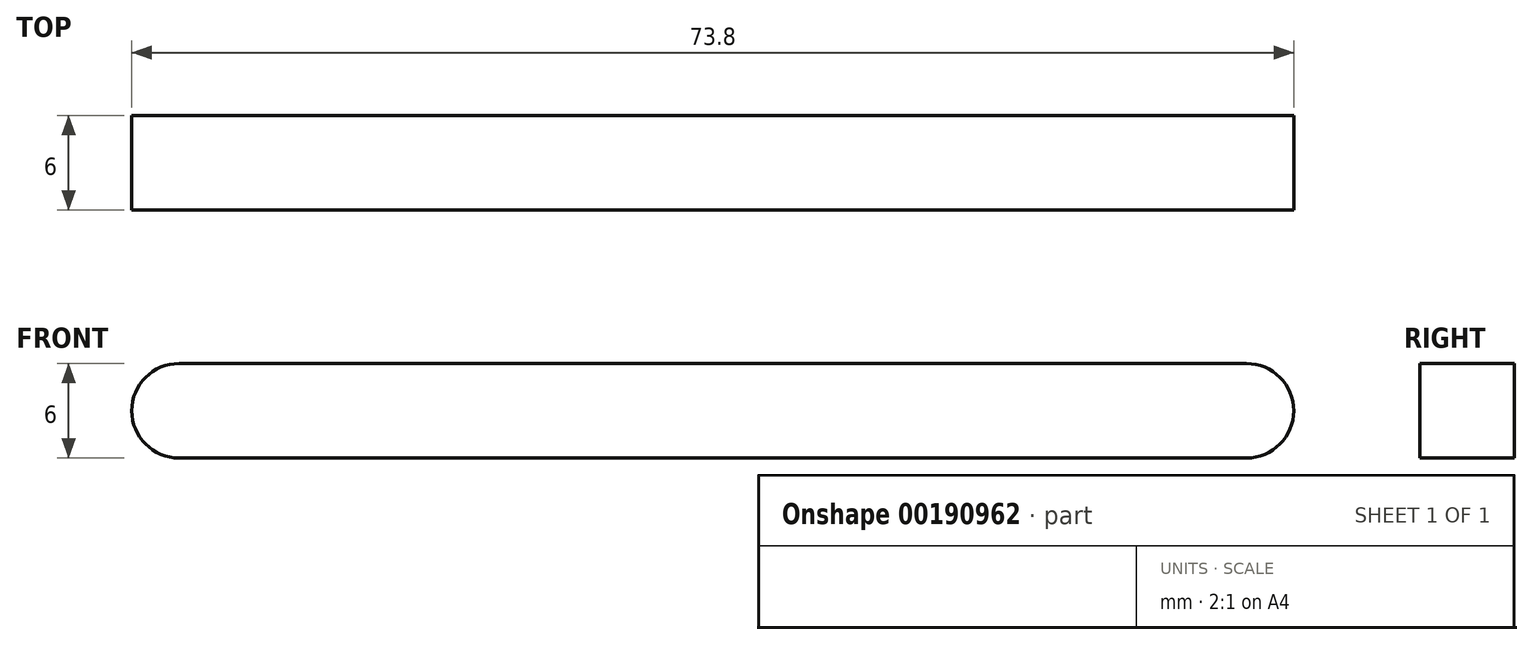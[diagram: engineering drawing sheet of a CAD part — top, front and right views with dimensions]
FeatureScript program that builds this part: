
annotation { "Feature Type Name" : "Feature", "Feature Type Description" : "" }
export const myFeature = defineFeature(function(context is Context, id is Id, definition is map)
    precondition{}
    {
        {
            var Q0;
            Q0=qCreatedBy(makeId("Front.planeOp"),FACE);
            var sketch = newSketch(context, id + "F0", { "sketchPlane" : qUnion([Q0])});
            skLineSegment(sketch, "E0.bottom", {"start": v(0, 0) * mm, "end": v(67.8, 0) * mm});
            skLineSegment(sketch, "E0.top", {"start": v(0, 6) * mm, "end": v(67.8, 6) * mm});
            skLineSegment(sketch, "E0.left", {"start": v(0, 0) * mm, "end": v(0, 6) * mm});
            skLineSegment(sketch, "E0.right", {"start": v(67.8, 0) * mm, "end": v(67.8, 6) * mm});
            skArc(sketch, "E1", {"start": v(67.8, 6) * mm, "mid": v(70.8, 3) * mm, "end": v(67.8, 0) * mm});
            skArc(sketch, "E2", {"start": v(0, 0) * mm, "mid": v(-3, 3) * mm, "end": v(0, 6) * mm});
            skSolve(sketch);
        }
        {
            var Q0;
            Q0=makeQuery(id+"F0.imprint","IMPRINT",FACE,{"disambiguationData":[TD([[makeQuery(id+"F0.imprint","IMPRINT",EDGE,{"derivedFrom":sQuery(id+"F0.wireOp",EDGE,"E0.bottom")}),1.0]])]});
            var Q1;
            Q1=makeQuery(id+"F0.imprint","IMPRINT",FACE,{"disambiguationData":[TD([[makeQuery(id+"F0.imprint","IMPRINT",EDGE,{"derivedFrom":sQuery(id+"F0.wireOp",EDGE,"E0.right")}),-1.0]])]});
            var Q2;
            Q2=makeQuery(id+"F0.imprint","IMPRINT",FACE,{"disambiguationData":[TD([[makeQuery(id+"F0.imprint","IMPRINT",EDGE,{"derivedFrom":sQuery(id+"F0.wireOp",EDGE,"E0.left")}),1.0]])]});
            extrude(context, id + "F1", {"entities" : qUnion([Q0, Q1, Q2]), "depth" : 6 * mm});
        }
    });
